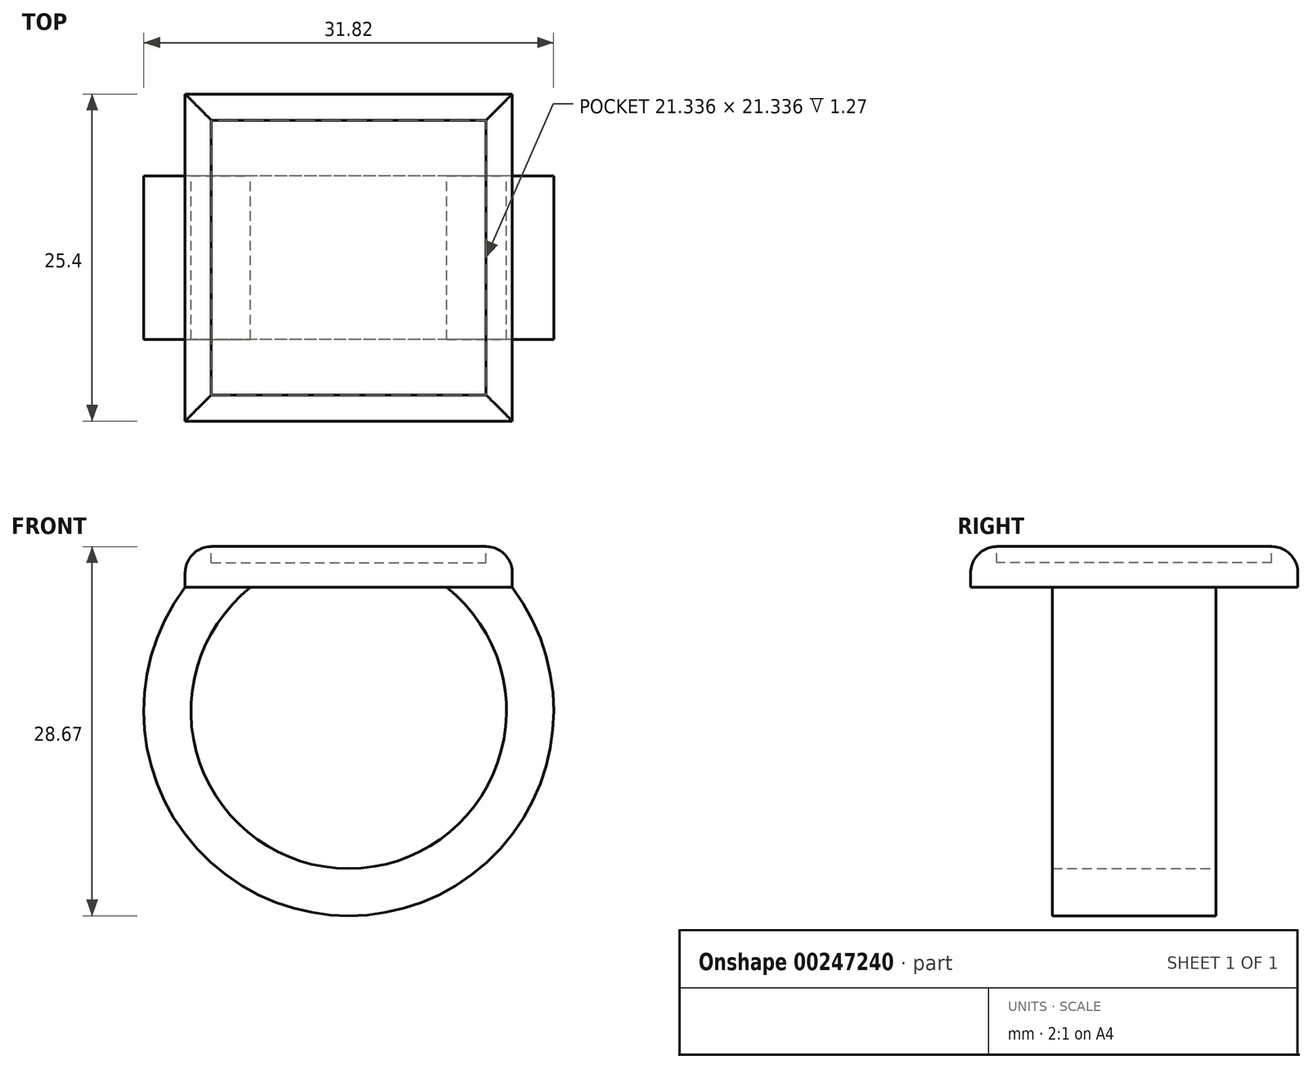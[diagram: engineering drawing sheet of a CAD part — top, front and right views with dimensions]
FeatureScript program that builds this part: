
annotation { "Feature Type Name" : "Feature", "Feature Type Description" : "" }
export const myFeature = defineFeature(function(context is Context, id is Id, definition is map)
    precondition{}
    {
        {
            var Q0;
            Q0=qCreatedBy(makeId("Top.planeOp"),FACE);
            var sketch = newSketch(context, id + "F0", { "sketchPlane" : qUnion([Q0])});
            skLineSegment(sketch, "E0.bottom", {"start": v(-12.7, 12.7) * mm, "end": v(12.7, 12.7) * mm});
            skLineSegment(sketch, "E0.top", {"start": v(-12.7, -12.7) * mm, "end": v(12.7, -12.7) * mm});
            skLineSegment(sketch, "E0.left", {"start": v(-12.7, 12.7) * mm, "end": v(-12.7, -12.7) * mm});
            skLineSegment(sketch, "E0.right", {"start": v(12.7, 12.7) * mm, "end": v(12.7, -12.7) * mm});
            skPoint(sketch, "E0.middle", {"position": v(0, 0) * mm});
            skSolve(sketch);
        }
        {
            var Q0;
            Q0=makeQuery(id+"F0.imprint","IMPRINT",FACE,{"disambiguationData":[TD([[makeQuery(id+"F0.imprint","IMPRINT",EDGE,{"derivedFrom":sQuery(id+"F0.wireOp",EDGE,"E0.bottom")}),-1.0]])]});
            extrude(context, id + "F1", {"entities" : qUnion([Q0]), "depth" : 3.17 * mm});
        }
        {
            var Q0;
            Q0=qCreatedBy(makeId("Front.planeOp"),FACE);
            var sketch = newSketch(context, id + "F2", { "sketchPlane" : qUnion([Q0])});
            skArc(sketch, "E1", {"start": v(-10.16, 0) * mm, "mid": v(0, -23.56) * mm, "end": v(10.16, 0) * mm});
            skSolve(sketch);
        }
        {
            var Q0;
            Q0=makeQuery(id+"F1.opExtrude","CAP_FACE",FACE,{"disambiguationData":[OSD([sQuery(id+"F0.wireOp",EDGE,"E0.bottom"),sQuery(id+"F0.wireOp",EDGE,"E0.top"),sQuery(id+"F0.wireOp",EDGE,"E0.left"),sQuery(id+"F0.wireOp",EDGE,"E0.right")])],"isStart":true});
            var sketch = newSketch(context, id + "F3", { "sketchPlane" : qUnion([Q0])});
            skLineSegment(sketch, "E2.bottom", {"start": v(12.7, 6.35) * mm, "end": v(7.62, 6.35) * mm});
            skLineSegment(sketch, "E2.top", {"start": v(12.7, -6.35) * mm, "end": v(7.62, -6.35) * mm});
            skLineSegment(sketch, "E2.left", {"start": v(12.7, 6.35) * mm, "end": v(12.7, -6.35) * mm});
            skLineSegment(sketch, "E2.right", {"start": v(7.62, 6.35) * mm, "end": v(7.62, -6.35) * mm});
            skPoint(sketch, "E2.middle", {"position": v(10.16, 0) * mm});
            skSolve(sketch);
        }
        {
            var Q0;
            Q0=makeQuery(id+"F3.imprint","IMPRINT",FACE,{"disambiguationData":[TD([[makeQuery(id+"F3.imprint","IMPRINT",EDGE,{"derivedFrom":sQuery(id+"F3.wireOp",EDGE,"E2.bottom")}),1.0]])]});
            var Q1;
            Q1 = qConstructionFilter(qBodyType(qCreatedBy(id + "F3" ,EDGE), BodyType.WIRE), ConstructionObject.NO);
            var Q2;
            Q2 = qConstructionFilter(qBodyType(qCreatedBy(id + "F2" ,EDGE), BodyType.WIRE), ConstructionObject.NO);
            sweep(context, id + "F4", {"profiles" : qUnion([Q0]), "surfaceProfiles" : qUnion([Q1]), "path" : qUnion([Q2])});
        }
        {
            var Q0;
            Q0=qCreatedBy(makeId("Front.planeOp"),FACE);
            var sketch = newSketch(context, id + "F5", { "sketchPlane" : qUnion([Q0])});
            skLineSegment(sketch, "E3.0", {"start": v(-12.7, 0) * mm, "end": v(12.7, 0) * mm});
            skSolve(sketch);
        }
        {
            var Q0;
            Q0=qCreatedBy(makeId("Front.planeOp"),FACE);
            var sketch = newSketch(context, id + "F6", { "sketchPlane" : qUnion([Q0])});
            skArc(sketch, "E4", {"start": v(-7.62, 0) * mm, "mid": v(-8.9, -1.18) * mm, "end": v(-10.01, -2.54) * mm});
            skLineSegment(sketch, "E5.0", {"start": v(-10.16, 0) * mm, "end": v(-7.62, 0) * mm});
            skLineSegment(sketch, "E6", {"start": v(-10.16, 0) * mm, "end": v(-10.01, -2.54) * mm});
            skPoint(sketch, "E7.orphan", {"position": v(-12.7, 0) * mm});
            skPoint(sketch, "E8.orphan", {"position": v(12.7, 0) * mm});
            skSolve(sketch);
        }
        {
            var Q0;
            Q0=makeQuery(id+"F6.imprint","IMPRINT",FACE,{"disambiguationData":[TD([[makeQuery(id+"F6.imprint","IMPRINT",EDGE,{"derivedFrom":sQuery(id+"F6.wireOp",EDGE,"E4")}),-1.0]])]});
            extrude(context, id + "F7", {"entities" : qUnion([Q0]), "operationType" : NewBodyOperationType.ADD, "endBound" : BoundingType.SYMMETRIC, "depth" : 12.7 * mm});
        }
        {
            var Q0;
            Q0=makeQuery(id+"F1.opExtrude","CAP_EDGE",EDGE,{"disambiguationData":[OSD([sQuery(id+"F0.wireOp",EDGE,"E0.left")])],"isStart":false});
            var Q1;
            Q1=makeQuery(id+"F1.opExtrude","CAP_EDGE",EDGE,{"disambiguationData":[OSD([sQuery(id+"F0.wireOp",EDGE,"E0.right")])],"isStart":false});
            var Q2;
            Q2=makeQuery(id+"F1.opExtrude","CAP_EDGE",EDGE,{"disambiguationData":[OSD([sQuery(id+"F0.wireOp",EDGE,"E0.top")])],"isStart":false});
            var Q3;
            Q3=makeQuery(id+"F1.opExtrude","CAP_EDGE",EDGE,{"disambiguationData":[OSD([sQuery(id+"F0.wireOp",EDGE,"E0.bottom")])],"isStart":false});
            fillet(context, id + "F8", {"entities" : qUnion([Q0, Q1, Q2, Q3]), "radius" : 2.03 * mm, "tangentPropagation" : true, "allowEdgeOverflow" : false});
        }
        {
            var Q0;
            Q0=makeQuery(id+"F1.opExtrude","CAP_FACE",FACE,{"disambiguationData":[OSD([sQuery(id+"F0.wireOp",EDGE,"E0.bottom"),sQuery(id+"F0.wireOp",EDGE,"E0.top"),sQuery(id+"F0.wireOp",EDGE,"E0.left"),sQuery(id+"F0.wireOp",EDGE,"E0.right")])],"isStart":false});
            extrude(context, id + "F9", {"entities" : qUnion([Q0]), "operationType" : NewBodyOperationType.REMOVE, "oppositeDirection" : true, "depth" : 1.27 * mm});
        }
    });
